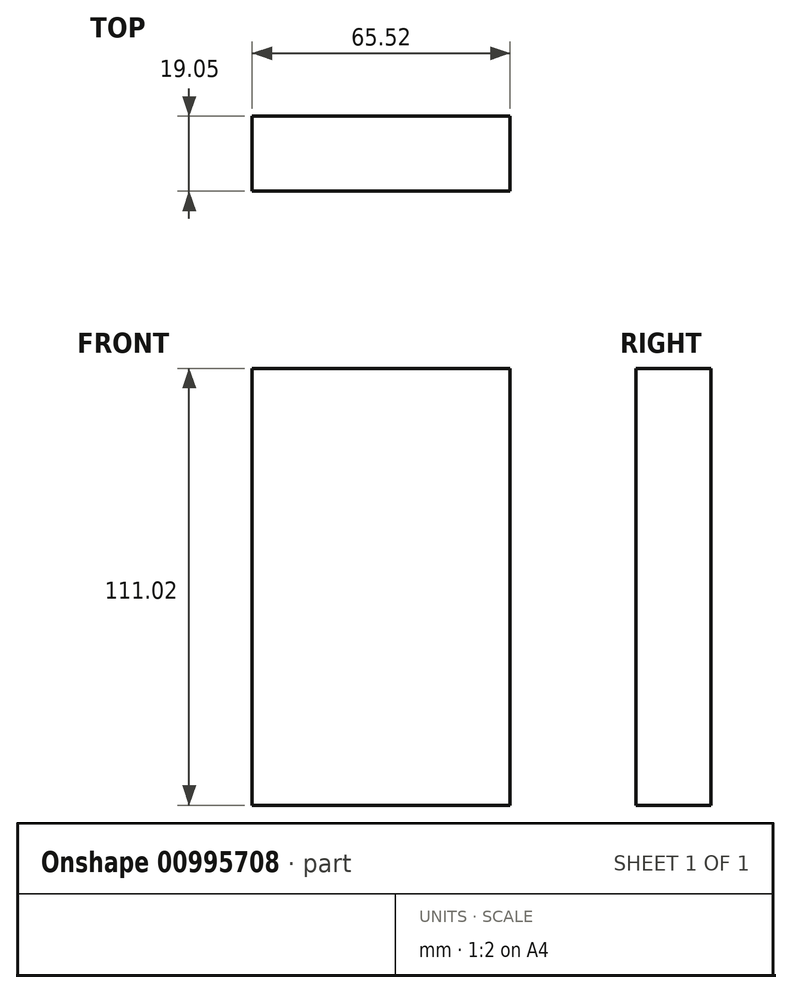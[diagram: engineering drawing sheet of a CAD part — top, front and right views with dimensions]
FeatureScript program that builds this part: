
annotation { "Feature Type Name" : "Feature", "Feature Type Description" : "" }
export const myFeature = defineFeature(function(context is Context, id is Id, definition is map)
    precondition{}
    {
        {
            var Q0;
            Q0=qCreatedBy(makeId("Front.planeOp"),FACE);
            var sketch = newSketch(context, id + "F0", { "sketchPlane" : qUnion([Q0])});
            skLineSegment(sketch, "E0.bottom", {"start": v(0, 0) * mm, "end": v(-65.52, 0) * mm});
            skLineSegment(sketch, "E0.top", {"start": v(0, 111.02) * mm, "end": v(-65.52, 111.02) * mm});
            skLineSegment(sketch, "E0.left", {"start": v(0, 0) * mm, "end": v(0, 111.02) * mm});
            skLineSegment(sketch, "E0.right", {"start": v(-65.52, 0) * mm, "end": v(-65.52, 111.02) * mm});
            skSolve(sketch);
        }
        {
            var Q0;
            Q0=makeQuery(id+"F0.imprint","IMPRINT",FACE,{"disambiguationData":[TD([[makeQuery(id+"F0.imprint","IMPRINT",EDGE,{"derivedFrom":sQuery(id+"F0.wireOp",EDGE,"E0.bottom")}),-1.0]])]});
            extrude(context, id + "F1", {"entities" : qUnion([Q0]), "depth" : 19.05 * mm, "offsetDistance" : 25.4 * mm});
        }
    });
